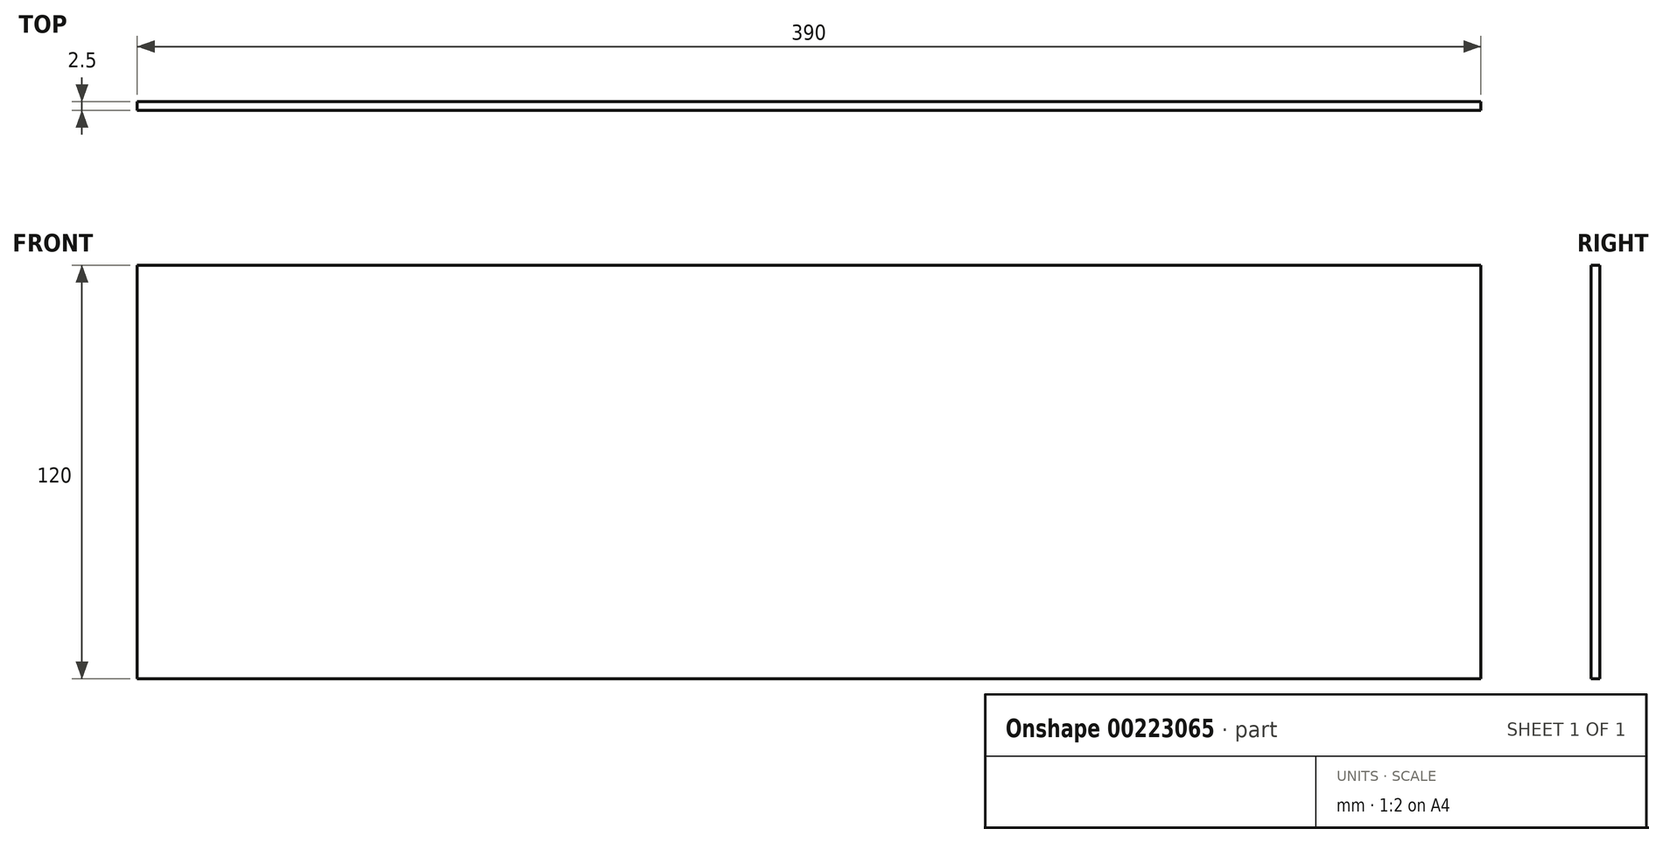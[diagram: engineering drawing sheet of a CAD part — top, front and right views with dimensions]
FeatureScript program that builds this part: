
annotation { "Feature Type Name" : "Feature", "Feature Type Description" : "" }
export const myFeature = defineFeature(function(context is Context, id is Id, definition is map)
    precondition{}
    {
        {
            var Q0;
            Q0=qCreatedBy(makeId("Front.planeOp"),FACE);
            var sketch = newSketch(context, id + "F0", { "sketchPlane" : qUnion([Q0])});
            skLineSegment(sketch, "E0.bottom", {"start": v(195, -60) * mm, "end": v(-195, -60) * mm});
            skLineSegment(sketch, "E0.top", {"start": v(195, 60) * mm, "end": v(-195, 60) * mm});
            skLineSegment(sketch, "E0.left", {"start": v(195, -60) * mm, "end": v(195, 60) * mm});
            skLineSegment(sketch, "E0.right", {"start": v(-195, -60) * mm, "end": v(-195, 60) * mm});
            skPoint(sketch, "E0.middle", {"position": v(0, 0) * mm});
            skSolve(sketch);
        }
        {
            var Q0;
            Q0=makeQuery(id+"F0.imprint","IMPRINT",FACE,{"disambiguationData":[TD([[makeQuery(id+"F0.imprint","IMPRINT",EDGE,{"derivedFrom":sQuery(id+"F0.wireOp",EDGE,"E0.bottom")}),-1.0]])]});
            extrude(context, id + "F1", {"entities" : qUnion([Q0]), "depth" : 2.5 * mm});
        }
    });
